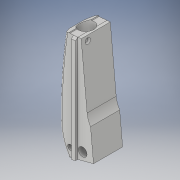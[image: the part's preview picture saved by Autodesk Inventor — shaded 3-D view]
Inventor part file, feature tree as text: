
AUTODESK INVENTOR PART (.ipt)
format: ipt  version: 2018.3 (Build 223284000, 284)  size: 259,072 bytes
history: native  units: in
note: dims shown in document units (in); Inventor stores cm internally (conversion verified against a paired STEP export)
features: extrude x4, sketch x3, chamfer x3, plane x2, fillet x1, hole x1
ambient origin geometry x8: Origin, YZ Plane, XZ Plane, XY Plane, X Axis, Y Axis, Z Axis, Center Point
bodies: Solid1 (feature_tree)
feature tree (14):
  sketch  "Sketch1"  dims[d20=0.0378in d21=0.21in]
  extrude  "Extrusion1"  Depth=0.21in
  plane  "Work Plane2"
  sketch  "Sketch3"  dims[d22=90.0deg d23=1.9in]
  extrude  "Extrusion3"  Depth=1.9in
  extrude  "Extrusion4"  Depth=0.05in
  extrude  "Extrusion5"  Depth=0.05in
  chamfer  "Chamfer1"  Distance=0.19in
  chamfer  "Chamfer2"  Distance=0.16in
  fillet  "Fillet2"  Radius=0.6803in
  chamfer  "Chamfer3"  Distance=0.376in
  plane  "Work Plane3"
  hole  "Hole1"  [1 undecoded]
  sketch  "Sketch6"  dims[d24=1.792in d25=1.14in d26=0.844in d27=0.19in d28=0.16in d29=0.6803in d30=0.376in d32=0.0378in d33=0.09in d35=22.5deg d37=1.765in d38=18.0in d39=0.9345in d40=1.94in d41=0.265in d42=0.044in d43=0.538in d44=0.0in d54=0.078in d55=0.0in d56=0.622in d57=0.622in d58=0.0in d59=0.0in d60=0.28in d61=0.174in d62=0.311in d63=1.672in d64=0.0in d65=0.0in d66=0.094in d67=0.233in d68=0.155in d69=0.7485in d70=0.0in d73=0.125in d74=0.125in d75=0.1718in d76=0.125in d77=0.125in d78=0.1718in d79=0.05in d80=0.04in d81=0.125in d82=0.1718in d94=0.0in d95=0.063in d96=0.088in d97=0.155in d98=0.063in d99=0.75in d100=0.099in d101=0.25in d102=60.0deg d103=1.0in d104=0.8108in]
note: 1 required parameter value undecoded (feature->parameter linkage not recoverable at this tier; creation-order binding heuristic only, values carry confidence <= 0.55)
